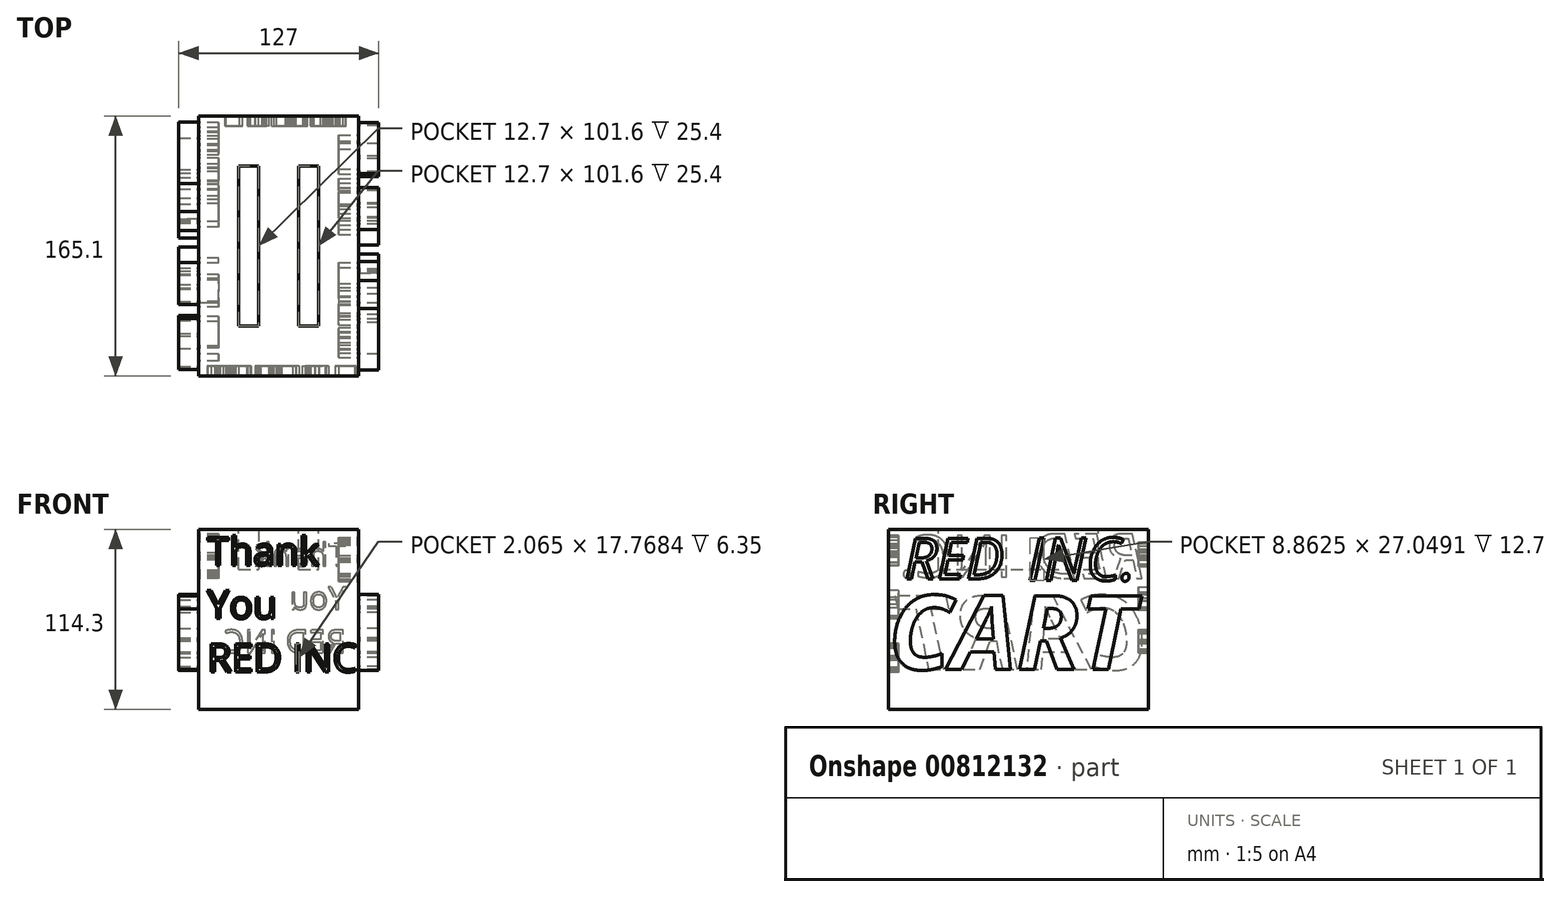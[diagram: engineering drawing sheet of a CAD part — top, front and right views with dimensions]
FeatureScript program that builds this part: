
annotation { "Feature Type Name" : "Feature", "Feature Type Description" : "" }
export const myFeature = defineFeature(function(context is Context, id is Id, definition is map)
    precondition{}
    {
        {
            var Q0;
            Q0=qCreatedBy(makeId("Front.planeOp"),FACE);
            var sketch = newSketch(context, id + "F0", { "sketchPlane" : qUnion([Q0])});
            skLineSegment(sketch, "E0", {"start": v(-38.1, 45.23) * mm, "end": v(-38.1, -43.67) * mm});
            skLineSegment(sketch, "E1", {"start": v(-38.1, -43.67) * mm, "end": v(0, -43.67) * mm});
            skLineSegment(sketch, "E2", {"start": v(0, -43.67) * mm, "end": v(0, 19.83) * mm});
            skLineSegment(sketch, "E3", {"start": v(0, 19.83) * mm, "end": v(-12.7, 19.83) * mm});
            skLineSegment(sketch, "E4", {"start": v(-12.7, 19.83) * mm, "end": v(-12.7, 45.23) * mm});
            skLineSegment(sketch, "E5", {"start": v(-12.7, 45.23) * mm, "end": v(-38.1, 45.23) * mm});
            skLineSegment(sketch, "E6", {"start": v(63.5, 45.23) * mm, "end": v(63.5, -43.67) * mm});
            skLineSegment(sketch, "E7", {"start": v(63.5, -43.67) * mm, "end": v(0, -43.67) * mm});
            skLineSegment(sketch, "E8", {"start": v(0, 19.83) * mm, "end": v(63.5, 19.83) * mm});
            skLineSegment(sketch, "E9", {"start": v(38.1, 19.83) * mm, "end": v(38.1, 45.23) * mm});
            skLineSegment(sketch, "E10", {"start": v(38.1, 45.23) * mm, "end": v(63.5, 45.23) * mm});
            skSolve(sketch);
        }
        {
            var Q0;
            Q0 = qSketchRegion(id + "F0", true);
            extrude(context, id + "F1", {"entities" : qUnion([Q0]), "endBound" : BoundingType.SYMMETRIC, "depth" : 165.1 * mm, "offsetDistance" : 25.4 * mm});
        }
        {
            var Q0;
            Q0=makeQuery(id+"F1.opExtrude","CAP_FACE",FACE,{"disambiguationData":[OSD([sQuery(id+"F0.wireOp",EDGE,"E0"),sQuery(id+"F0.wireOp",EDGE,"E1"),sQuery(id+"F0.wireOp",EDGE,"E3"),sQuery(id+"F0.wireOp",EDGE,"E4"),sQuery(id+"F0.wireOp",EDGE,"E5"),sQuery(id+"F0.wireOp",EDGE,"E6"),sQuery(id+"F0.wireOp",EDGE,"E7"),sQuery(id+"F0.wireOp",EDGE,"E8"),sQuery(id+"F0.wireOp",EDGE,"E9"),sQuery(id+"F0.wireOp",EDGE,"E10")])],"isStart":false});
            var sketch = newSketch(context, id + "F2", { "sketchPlane" : qUnion([Q0])});
            skLineSegment(sketch, "E11", {"start": v(0, 19.83) * mm, "end": v(0, 45.23) * mm});
            skLineSegment(sketch, "E12", {"start": v(0, 45.23) * mm, "end": v(25.4, 45.23) * mm});
            skLineSegment(sketch, "E13", {"start": v(25.4, 45.23) * mm, "end": v(25.4, 19.83) * mm});
            skSolve(sketch);
        }
        {
            var Q0;
            {var subQ0=sQuery(id+"F2.wireOp",EDGE,"E11");Q0=makeQuery(id+"F2.imprint","IMPRINT",FACE,{"disambiguationData":[TD([[makeQuery(id+"F2.imprint","IMPRINT",EDGE,{"derivedFrom":subQ0}),-1.0]])]});}
            extrude(context, id + "F3", {"entities" : qUnion([Q0]), "operationType" : NewBodyOperationType.ADD, "oppositeDirection" : true, "depth" : 165.1 * mm, "offsetDistance" : 25.4 * mm});
        }
        {
            var Q0;
            Q0=makeQuery(id+"F1.opExtrude","SWEPT_FACE",FACE,{"disambiguationData":[OSD([sQuery(id+"F0.wireOp",EDGE,"E6")])]});
            var sketch = newSketch(context, id + "F4", { "sketchPlane" : qUnion([Q0])});
            skLineSegment(sketch, "E14", {"start": v(-82.55, 45.23) * mm, "end": v(-50.8, 45.23) * mm});
            skLineSegment(sketch, "E15", {"start": v(-50.8, 45.23) * mm, "end": v(-50.8, 19.83) * mm});
            skLineSegment(sketch, "E16", {"start": v(-50.8, 19.83) * mm, "end": v(-82.55, 19.83) * mm});
            skLineSegment(sketch, "E17", {"start": v(-82.55, 19.83) * mm, "end": v(-82.55, 45.23) * mm});
            skLineSegment(sketch, "E18.MirrorCS", {"start": v(50.8, 45.23) * mm, "end": v(50.8, 19.83) * mm});
            skLineSegment(sketch, "E19.MirrorCS", {"start": v(82.55, 45.23) * mm, "end": v(50.8, 45.23) * mm});
            skLineSegment(sketch, "E20.MirrorCS", {"start": v(82.55, 19.83) * mm, "end": v(82.55, 45.23) * mm});
            skLineSegment(sketch, "E21.MirrorCS", {"start": v(50.8, 19.83) * mm, "end": v(82.55, 19.83) * mm});
            skSolve(sketch);
        }
        {
            var Q0;
            Q0 = qSketchRegion(id + "F4", true);
            extrude(context, id + "F5", {"entities" : qUnion([Q0]), "operationType" : NewBodyOperationType.ADD, "oppositeDirection" : true, "depth" : 101.6 * mm, "offsetDistance" : 25.4 * mm});
        }
        {
            var Q0;
            Q0=makeQuery(id+"F1.opExtrude","SWEPT_FACE",FACE,{"disambiguationData":[OSD([sQuery(id+"F0.wireOp",EDGE,"E6")])]});
            var sketch = newSketch(context, id + "F6", { "sketchPlane" : qUnion([Q0])});
            skText(sketch, "E22", { "text": "CART", "fontName": "OpenSans-BoldItalic.ttf"});
            const initialGuessF6  = {"E22": [-0.08255, -0.04367, 1, 0, 0.04725]};
            skSetInitialGuess(sketch, initialGuessF6);
            skSolve(sketch);
        }
        {
            var Q0;
            Q0 = qSketchRegion(id + "F6", true);
            extrude(context, id + "F7", {"entities" : qUnion([Q0]), "operationType" : NewBodyOperationType.ADD, "depth" : 12.7 * mm, "offsetDistance" : 25.4 * mm});
        }
        {
            var Q0;
            Q0=makeQuery(id+"F1.opExtrude","SWEPT_FACE",FACE,{"disambiguationData":[OSD([sQuery(id+"F0.wireOp",EDGE,"E0")])]});
            var sketch = newSketch(context, id + "F8", { "sketchPlane" : qUnion([Q0])});
            skText(sketch, "E23", { "text": "CART", "fontName": "OpenSans-BoldItalic.ttf"});
            const initialGuessF8  = {"E23": [-0.08255, -0.04367, 1, 0, 0.04725]};
            skSetInitialGuess(sketch, initialGuessF8);
            skSolve(sketch);
        }
        {
            var Q0;
            Q0 = qSketchRegion(id + "F8", true);
            extrude(context, id + "F9", {"entities" : qUnion([Q0]), "operationType" : NewBodyOperationType.ADD, "depth" : 12.7 * mm, "offsetDistance" : 25.4 * mm});
        }
        {
            var Q0;
            {var subQ21=sQuery(id+"F0.wireOp",EDGE,"E5");var subQ24=sQuery(id+"F0.wireOp",EDGE,"E0");Q0=makeQuery(id+"F9.boolean.opBoolean","SPLIT",FACE,{"disambiguationData":[TD([makeQuery(id+"F1.opExtrude","SWEPT_FACE",FACE,{"disambiguationData":[OSD([subQ21])]})])],"derivedFrom":makeQuery(id+"F1.opExtrude","SWEPT_FACE",FACE,{"disambiguationData":[OSD([subQ24])]})});}
            var sketch = newSketch(context, id + "F10", { "sketchPlane" : qUnion([Q0])});
            skText(sketch, "E24", { "text": "RED", "fontName": "OpenSans-Italic.ttf"});
            skText(sketch, "E25", { "text": "INC.", "fontName": "OpenSans-Regular.ttf"});
            const initialGuessF10  = {"E24": [-0.08014, 0.01416, 1, 0, 0.02858], "E25": [0.00403, 0.01494, 1, 0, 0.02676]};
            skSetInitialGuess(sketch, initialGuessF10);
            skSolve(sketch);
        }
        {
            var Q0;
            Q0 = qSketchRegion(id + "F10", true);
            extrude(context, id + "F11", {"entities" : qUnion([Q0]), "operationType" : NewBodyOperationType.REMOVE, "oppositeDirection" : true, "depth" : 12.7 * mm, "offsetDistance" : 25.4 * mm});
        }
        {
            var Q0;
            {var subQ1=sQuery(id+"F0.wireOp",EDGE,"E5");var subQ28=sQuery(id+"F0.wireOp",EDGE,"E6");Q0=makeQuery(id+"F7.boolean.opBoolean","SPLIT",FACE,{"disambiguationData":[TD([makeQuery(id+"F1.opExtrude","SWEPT_FACE",FACE,{"disambiguationData":[OSD([subQ1])]})])],"derivedFrom":makeQuery(id+"F1.opExtrude","SWEPT_FACE",FACE,{"disambiguationData":[OSD([subQ28])]})});}
            var sketch = newSketch(context, id + "F12", { "sketchPlane" : qUnion([Q0])});
            skText(sketch, "E26", { "text": "RED", "fontName": "OpenSans-Italic.ttf"});
            skText(sketch, "E27", { "text": "INC.", "fontName": "OpenSans-Italic.ttf"});
            const initialGuessF12  = {"E26": [-0.07235, 0.0139, 1, 0, 0.02598], "E27": [0.00584, 0.01286, 1, 0, 0.02728]};
            skSetInitialGuess(sketch, initialGuessF12);
            skSolve(sketch);
        }
        {
            var Q0;
            Q0 = qSketchRegion(id + "F12", true);
            extrude(context, id + "F13", {"entities" : qUnion([Q0]), "operationType" : NewBodyOperationType.REMOVE, "oppositeDirection" : true, "depth" : 12.7 * mm, "offsetDistance" : 25.4 * mm});
        }
        {
            var Q0;
            Q0=makeQuery(id+"F9.boolean.opBoolean","MERGE",FACE,{"derivedFrom":[makeQuery(id+"F7.boolean.opBoolean","MERGE",FACE,{"derivedFrom":[makeQuery(id+"F1.opExtrude","SWEPT_FACE",FACE,{"disambiguationData":[OSD([sQuery(id+"F0.wireOp",EDGE,"E1"),sQuery(id+"F0.wireOp",EDGE,"E7")])]}),makeQuery(id+"F7.opExtrude","SWEPT_FACE",FACE,{"disambiguationData":[OSD([sQuery(id+"F6.wireOp",EDGE,"E22.sketch_text.stroke-20")])]}),makeQuery(id+"F7.opExtrude","SWEPT_FACE",FACE,{"disambiguationData":[OSD([sQuery(id+"F6.wireOp",EDGE,"E22.sketch_text.stroke-24")])]}),makeQuery(id+"F7.opExtrude","SWEPT_FACE",FACE,{"disambiguationData":[OSD([sQuery(id+"F6.wireOp",EDGE,"E22.sketch_text.stroke-40")])]}),makeQuery(id+"F7.opExtrude","SWEPT_FACE",FACE,{"disambiguationData":[OSD([sQuery(id+"F6.wireOp",EDGE,"E22.sketch_text.stroke-48")])]}),makeQuery(id+"F7.opExtrude","SWEPT_FACE",FACE,{"disambiguationData":[OSD([sQuery(id+"F6.wireOp",EDGE,"E22.sketch_text.stroke-51")])]})]}),makeQuery(id+"F9.opExtrude","SWEPT_FACE",FACE,{"disambiguationData":[OSD([sQuery(id+"F8.wireOp",EDGE,"E23.sketch_text.stroke-20")])]}),makeQuery(id+"F9.opExtrude","SWEPT_FACE",FACE,{"disambiguationData":[OSD([sQuery(id+"F8.wireOp",EDGE,"E23.sketch_text.stroke-24")])]}),makeQuery(id+"F9.opExtrude","SWEPT_FACE",FACE,{"disambiguationData":[OSD([sQuery(id+"F8.wireOp",EDGE,"E23.sketch_text.stroke-40")])]}),makeQuery(id+"F9.opExtrude","SWEPT_FACE",FACE,{"disambiguationData":[OSD([sQuery(id+"F8.wireOp",EDGE,"E23.sketch_text.stroke-48")])]}),makeQuery(id+"F9.opExtrude","SWEPT_FACE",FACE,{"disambiguationData":[OSD([sQuery(id+"F8.wireOp",EDGE,"E23.sketch_text.stroke-51")])]})]});
            var sketch = newSketch(context, id + "F14", { "sketchPlane" : qUnion([Q0])});
            skLineSegment(sketch, "E28", {"start": v(-38.1, 82.55) * mm, "end": v(-38.1, -82.55) * mm});
            skLineSegment(sketch, "E29", {"start": v(-38.1, -82.55) * mm, "end": v(63.5, -82.55) * mm});
            skLineSegment(sketch, "E30", {"start": v(63.5, -82.55) * mm, "end": v(63.5, 82.55) * mm});
            skLineSegment(sketch, "E31", {"start": v(63.5, 82.55) * mm, "end": v(-38.1, 82.55) * mm});
            skSolve(sketch);
        }
        {
            var Q0;
            Q0 = qSketchRegion(id + "F14", true);
            extrude(context, id + "F15", {"entities" : qUnion([Q0]), "operationType" : NewBodyOperationType.ADD, "depth" : 25.4 * mm, "offsetDistance" : 25.4 * mm});
        }
        {
            var Q0;
            {var subQ0=sQuery(id+"F0.wireOp",EDGE,"E8");var subQ1=sQuery(id+"F0.wireOp",EDGE,"E3");Q0=makeQuery(id+"F15.boolean.opBoolean","MERGE",FACE,{"derivedFrom":[makeQuery(id+"F5.boolean.opBoolean","MERGE",FACE,{"derivedFrom":[makeQuery(id+"F3.boolean.opBoolean","MERGE",FACE,{"derivedFrom":[makeQuery(id+"F1.opExtrude","CAP_FACE",FACE,{"disambiguationData":[OSD([sQuery(id+"F0.wireOp",EDGE,"E0"),sQuery(id+"F0.wireOp",EDGE,"E1"),subQ1,sQuery(id+"F0.wireOp",EDGE,"E4"),sQuery(id+"F0.wireOp",EDGE,"E5"),sQuery(id+"F0.wireOp",EDGE,"E6"),sQuery(id+"F0.wireOp",EDGE,"E7"),subQ0,sQuery(id+"F0.wireOp",EDGE,"E9"),sQuery(id+"F0.wireOp",EDGE,"E10")])],"isStart":false}),makeQuery(id+"F3.opExtrude","CAP_FACE",FACE,{"disambiguationData":[OSD([subQ1,subQ0,sQuery(id+"F2.wireOp",EDGE,"E11"),sQuery(id+"F2.wireOp",EDGE,"E12"),sQuery(id+"F2.wireOp",EDGE,"E13")])],"isStart":true})]}),makeQuery(id+"F5.opExtrude","SWEPT_FACE",FACE,{"disambiguationData":[OSD([sQuery(id+"F4.wireOp",EDGE,"E17")])]})]}),makeQuery(id+"F15.opExtrude","SWEPT_FACE",FACE,{"disambiguationData":[OSD([sQuery(id+"F14.wireOp",EDGE,"E31")])]})]});}
            var sketch = newSketch(context, id + "F16", { "sketchPlane" : qUnion([Q0])});
            skText(sketch, "E32", { "text": "Thank\nYou\nRED INC.", "fontName": "OpenSans-Regular.ttf"});
            const initialGuessF16  = {"E32": [-0.0326, 0.02247, 1, 0, 0.01792]};
            skSetInitialGuess(sketch, initialGuessF16);
            skSolve(sketch);
        }
        {
            var Q0;
            Q0 = qSketchRegion(id + "F16", true);
            extrude(context, id + "F17", {"entities" : qUnion([Q0]), "operationType" : NewBodyOperationType.REMOVE, "oppositeDirection" : true, "depth" : 6.35 * mm, "offsetDistance" : 25.4 * mm});
        }
        {
            var Q0;
            {var subQ0=sQuery(id+"F0.wireOp",EDGE,"E8");var subQ1=sQuery(id+"F0.wireOp",EDGE,"E3");Q0=makeQuery(id+"F15.boolean.opBoolean","MERGE",FACE,{"derivedFrom":[makeQuery(id+"F5.boolean.opBoolean","MERGE",FACE,{"derivedFrom":[makeQuery(id+"F3.boolean.opBoolean","MERGE",FACE,{"derivedFrom":[makeQuery(id+"F1.opExtrude","CAP_FACE",FACE,{"disambiguationData":[OSD([sQuery(id+"F0.wireOp",EDGE,"E0"),sQuery(id+"F0.wireOp",EDGE,"E1"),subQ1,sQuery(id+"F0.wireOp",EDGE,"E4"),sQuery(id+"F0.wireOp",EDGE,"E5"),sQuery(id+"F0.wireOp",EDGE,"E6"),sQuery(id+"F0.wireOp",EDGE,"E7"),subQ0,sQuery(id+"F0.wireOp",EDGE,"E9"),sQuery(id+"F0.wireOp",EDGE,"E10")])],"isStart":true}),makeQuery(id+"F3.opExtrude","CAP_FACE",FACE,{"disambiguationData":[OSD([subQ1,subQ0,sQuery(id+"F2.wireOp",EDGE,"E11"),sQuery(id+"F2.wireOp",EDGE,"E12"),sQuery(id+"F2.wireOp",EDGE,"E13")])],"isStart":false})]}),makeQuery(id+"F5.opExtrude","SWEPT_FACE",FACE,{"disambiguationData":[OSD([sQuery(id+"F4.wireOp",EDGE,"E20.MirrorCS")])]})]}),makeQuery(id+"F15.opExtrude","SWEPT_FACE",FACE,{"disambiguationData":[OSD([sQuery(id+"F14.wireOp",EDGE,"E29")])]})]});}
            var sketch = newSketch(context, id + "F18", { "sketchPlane" : qUnion([Q0])});
            skText(sketch, "E33", { "text": "Thank\nYou\nRED INC", "fontName": "OpenSans-Regular.ttf"});
            const initialGuessF18  = {"E33": [-0.05546, 0.02195, 1, 0, 0.01455]};
            skSetInitialGuess(sketch, initialGuessF18);
            skSolve(sketch);
        }
        {
            var Q0;
            Q0 = qSketchRegion(id + "F18", true);
            extrude(context, id + "F19", {"entities" : qUnion([Q0]), "operationType" : NewBodyOperationType.REMOVE, "oppositeDirection" : true, "depth" : 6.35 * mm, "offsetDistance" : 25.4 * mm});
        }
    });
